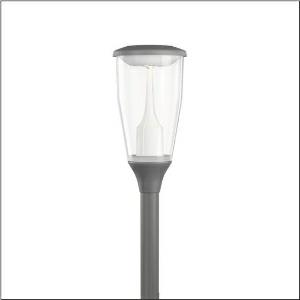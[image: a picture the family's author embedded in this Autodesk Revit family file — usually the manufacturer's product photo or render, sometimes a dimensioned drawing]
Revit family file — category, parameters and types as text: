
# Revit family: dl_11_iq___p1_0a_5xa5565bf14hp00022_ddba
name_source: partatom
category: Lighting Fixtures
units: mm (PartAtom-declared; Revit-internal decimal feet)

## family parameters
Cut with Voids When Loaded = No
Host = Face
Light Source = No
Part Type = Normal
Room Calculation Point = No
Round Connector Dimension = Use Diameter
Shared = No

## types (1)
- --- (1 x LED, 3950 lm, 33.6 W, 2200K)
    Apparent Load = 34 VA
    CIE Flux Codes = 33 63 91 94 100
    Color Rendering = 70
    Color Temperature = 2200K
    Default Elevation = 1800 mm
    Description = DL 11 iQ, mast luminaire, Module 540 iQ-SR, primary light control with 3 zone facetted reflector, of plastic, silver coated, highly specular, structured, primary optical cover: cover, of PMMA, transparent, light distribution: P1.0a, light emission: direct distribution, primary light characteristic: asymmetric, installation type: post-top, LED, High Power LED, light colour: 722, colour temperature: 2200K, control gear: iQ Street-Remote, control: Street-Remote, Auto-Match, Temp-Guard, Lumen-Switch, Night-Set, Smart-Wire, Light-Fading, Desk-Remote (wireless, voltage-free reading and setting of iQ features in the workshop via application-optimized NFC function/RFID function), optimised constant luminous flux control (CLO 2.0), mains connection: 220..240V, AC, 50/60Hz, connection cable pre-assembled, cable length: 5,5m, start of lifetime: 34W, end of service life: 36W, luminaire housing, upper part, of diecast aluminium, coated, Siteco® metallic grey (DB 702S), spigot size: 60mm (post-top), mounting height: 3..5m, post-top mast mounting element, of diecast aluminium, coated, Siteco® metallic grey (DB 702S), Module 540 iQ-SR, traffic white (RAL 9016), equipment: Power, protection rating (complete): IP66, insulation class (complete): insulation class II (safety insulation), certification: CE, ENEC, ENEC+, VDE, impact resistance: IK07, packaging unit: 1 piece

Light Distribution: P1.0a
    Height = 665 mm
    Lamp = 1 x LED
    Lamp Light Flux = 3950 lm
    Lamp Power = 33.6 W
    Lamp count = 1
    Length = 334 mm
    Luminous efficacy = 118 lm/W
    Manufacturer = Siteco
    ModVariant = No
    Model = 5XA5565BF14HP00022
    Number of Poles = 1
    OnlyDefault = Yes
    Power Factor = 1
    Product Name = DL 11 iQ | P1.0a
    Product group = mast luminaire | pylon top
    ProductGroupID = 6100
    Protection Class = Protection class II
    Protection Degree = IP 66
    RLX_Detail_Level = 1
    RLX_Emergency_Light_Flux = 0 lm
    RLX_Emergency_Type = 0
    RLX_Emergency_Type_DB = No
    RlxData = <blob elided: 104933 chars, md5=e5b9810d>
    Socket = socket
    Standby Power = 0 W
    System Light Flux = 3950 lm
    System Power = 34 W
    Type Comments = factory setting: luminous flux: 100 % | dim-lin: 254 | 695 mA
    Type Image = l_1258354.jpg
    URL = http://relux.com
    VarID = @adj_053443
    Voltage = 0 V
    Weight = 0.00 kg
    Width = 0 mm  [stored 0 ft]

note: [stored X ft] marks values corroborated as IEEE doubles in the binary element streams (Revit-internal decimal feet)

## geometry (parser evidence)
native form markers: Blend x4, Sweep x9
no freeform markers — native parametric forms only
